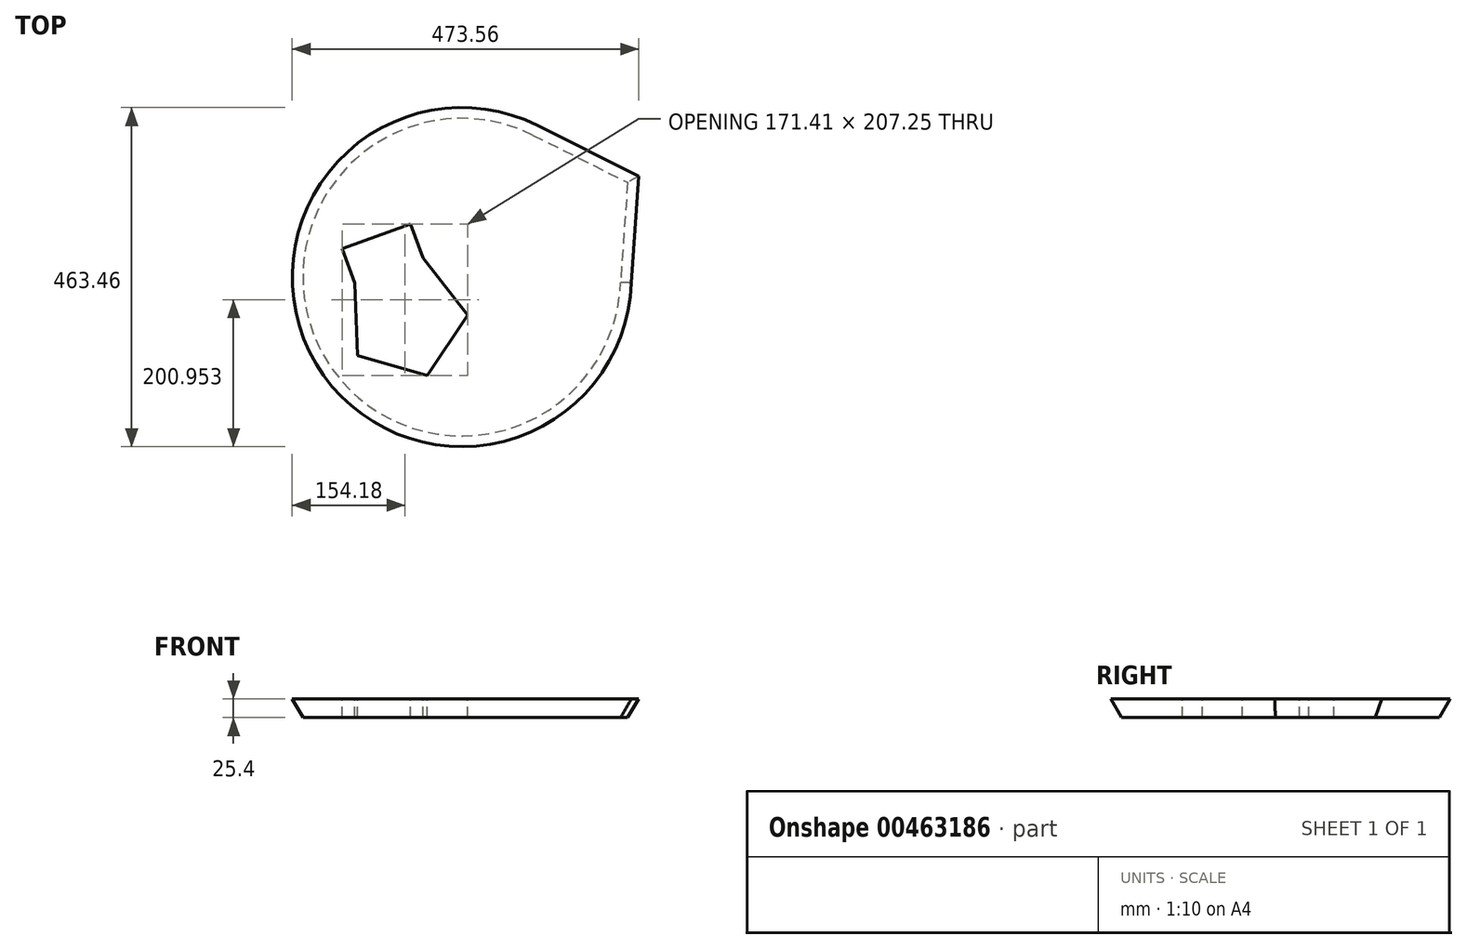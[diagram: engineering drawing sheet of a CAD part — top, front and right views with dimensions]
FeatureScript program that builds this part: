
annotation { "Feature Type Name" : "Feature", "Feature Type Description" : "" }
export const myFeature = defineFeature(function(context is Context, id is Id, definition is map)
    precondition{}
    {
        {
            var Q0;
            Q0=qCreatedBy(makeId("Top.planeOp"),FACE);
            var sketch = newSketch(context, id + "F0", { "sketchPlane" : qUnion([Q0])});
            skCircle(sketch, "E0", {"center": v(-91.12, -6.6) * mm, "radius": 47.15 * mm});
            skPoint(sketch, "E0.first.point", {"position": v(-124.21, 27) * mm});
            skPoint(sketch, "E0.second.point", {"position": v(-116.6, -46.26) * mm});
            skPoint(sketch, "E0.third.point", {"position": v(-44.1, -10.18) * mm});
            skSolve(sketch);
        }
        {
            var Q0;
            Q0=makeQuery(id+"F0.imprint","IMPRINT",FACE,{"disambiguationData":[TD([[makeQuery(id+"F0.imprint","IMPRINT",EDGE,{"derivedFrom":sQuery(id+"F0.wireOp",EDGE,"E0")}),1.0]])]});
            var Q1;
            Q1=sQuery(id+"F0.wireOp",EDGE,"E0");
            extrude(context, id + "F1", {"entities" : qUnion([Q0]), "bodyType" : ToolBodyType.SURFACE, "surfaceEntities" : qUnion([Q1]), "depth" : 75.44 * mm, "hasDraft" : true, "draftAngle" : 30 * degree});
        }
        {
            var Q0;
            Q0=qCreatedBy(makeId("Top.planeOp"),FACE);
            var sketch = newSketch(context, id + "F2", { "sketchPlane" : qUnion([Q0])});
            skLineSegment(sketch, "E1", {"start": v(215.15, -92.4) * mm, "end": v(224.73, 44.16) * mm});
            skLineSegment(sketch, "E2", {"start": v(224.73, 44.16) * mm, "end": v(95.32, 108.9) * mm});
            skArc(sketch, "E3", {"start": v(95.32, 108.9) * mm, "mid": v(-188.3, -196.27) * mm, "end": v(215.15, -92.4) * mm});
            skSolve(sketch);
        }
        {
            var Q0;
            Q0=makeQuery(id+"F2.imprint","IMPRINT",FACE,{"disambiguationData":[TD([[makeQuery(id+"F2.imprint","IMPRINT",EDGE,{"derivedFrom":sQuery(id+"F2.wireOp",EDGE,"E1")}),1.0]])]});
            var Q1;
            Q1=sQuery(id+"F2.wireOp",EDGE,"E2");
            var Q2;
            Q2=sQuery(id+"F2.wireOp",EDGE,"E3");
            var Q3;
            Q3=sQuery(id+"F2.wireOp",EDGE,"E1");
            extrude(context, id + "F3", {"entities" : qUnion([Q0]), "surfaceEntities" : qUnion([Q1, Q2, Q3]), "depth" : 25.4 * mm, "hasDraft" : true, "draftAngle" : 30 * degree});
        }
        {
            var Q0;
            Q0=makeQuery(id+"F3.opExtrude","CAP_FACE",FACE,{"disambiguationData":[OSD([sQuery(id+"F2.wireOp",EDGE,"E1"),sQuery(id+"F2.wireOp",EDGE,"E2"),sQuery(id+"F2.wireOp",EDGE,"E3")])],"isStart":false});
            var sketch = newSketch(context, id + "F4", { "sketchPlane" : qUnion([Q0])});
            skCircle(sketch, "E4.cCircle", {"center": v(-78, -140.32) * mm, "radius": 68.3 * mm, "construction": true});
            skLineSegment(sketch, "E4.0", {"start": v(-49.1, -219.64) * mm, "end": v(-144.5, -192.32) * mm});
            skLineSegment(sketch, "E4.1", {"start": v(-144.5, -192.32) * mm, "end": v(-148, -93.14) * mm});
            skLineSegment(sketch, "E4.2", {"start": v(-148, -93.14) * mm, "end": v(-54.76, -59.17) * mm});
            skLineSegment(sketch, "E4.3", {"start": v(-54.76, -59.17) * mm, "end": v(6.36, -137.35) * mm});
            skLineSegment(sketch, "E4.4", {"start": v(6.36, -137.35) * mm, "end": v(-49.1, -219.64) * mm});
            skPoint(sketch, "E4.0.midPoint", {"position": v(-96.8, -205.98) * mm});
            skSolve(sketch);
        }
        {
            var Q0;
            Q0=makeQuery(id+"F4.imprint","IMPRINT",FACE,{"disambiguationData":[TD([[makeQuery(id+"F4.imprint","IMPRINT",EDGE,{"derivedFrom":sQuery(id+"F4.wireOp",EDGE,"E4.0")}),-1.0]])]});
            extrude(context, id + "F5", {"entities" : qUnion([Q0]), "operationType" : NewBodyOperationType.REMOVE, "oppositeDirection" : true, "depth" : 74.42 * mm, "offsetDistance" : 25.4 * mm});
        }
        {
            var Q0;
            Q0=makeQuery(id+"F5.boolean.opBoolean","COPY",FACE,{"derivedFrom":makeQuery(id+"F5.opExtrude","SWEPT_FACE",FACE,{"disambiguationData":[OSD([sQuery(id+"F4.wireOp",EDGE,"E4.2")])]})});
            extrude(context, id + "F6", {"entities" : qUnion([Q0]), "operationType" : NewBodyOperationType.REMOVE, "oppositeDirection" : true, "depth" : 49.78 * mm, "offsetDistance" : 25.4 * mm});
        }
    });
